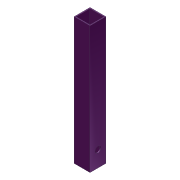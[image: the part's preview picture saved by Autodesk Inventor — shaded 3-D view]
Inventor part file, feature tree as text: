
AUTODESK INVENTOR PART (.ipt)
format: ipt  version: 2012 (Build 160160000, 160)  size: 89,600 bytes
history: native  units: in
note: dims shown in document units (in); Inventor stores cm internally (conversion verified against a paired STEP export)
features: extrude x2, sketch x2, shell x1
ambient origin geometry x8: Origin, YZ Plane, XZ Plane, XY Plane, X Axis, Y Axis, Z Axis, Center Point
bodies: Solid1 (feature_tree)
feature tree (5):
  extrude  "Extrusion1"  Depth=1.0in
  shell  "Shell1"  Thickness=1.0in
  extrude  "Extrusion2"  Depth=1.0in
  sketch  "Sketch1"  dims[d0=8.0in d1=1.0in d2=1.0in d3=0.0in]
  sketch  "Sketch2"  dims[d4=0.0625in d5=1.0in d6=0.5in d7=0.375in d8=1.0in d9=0.0in]
